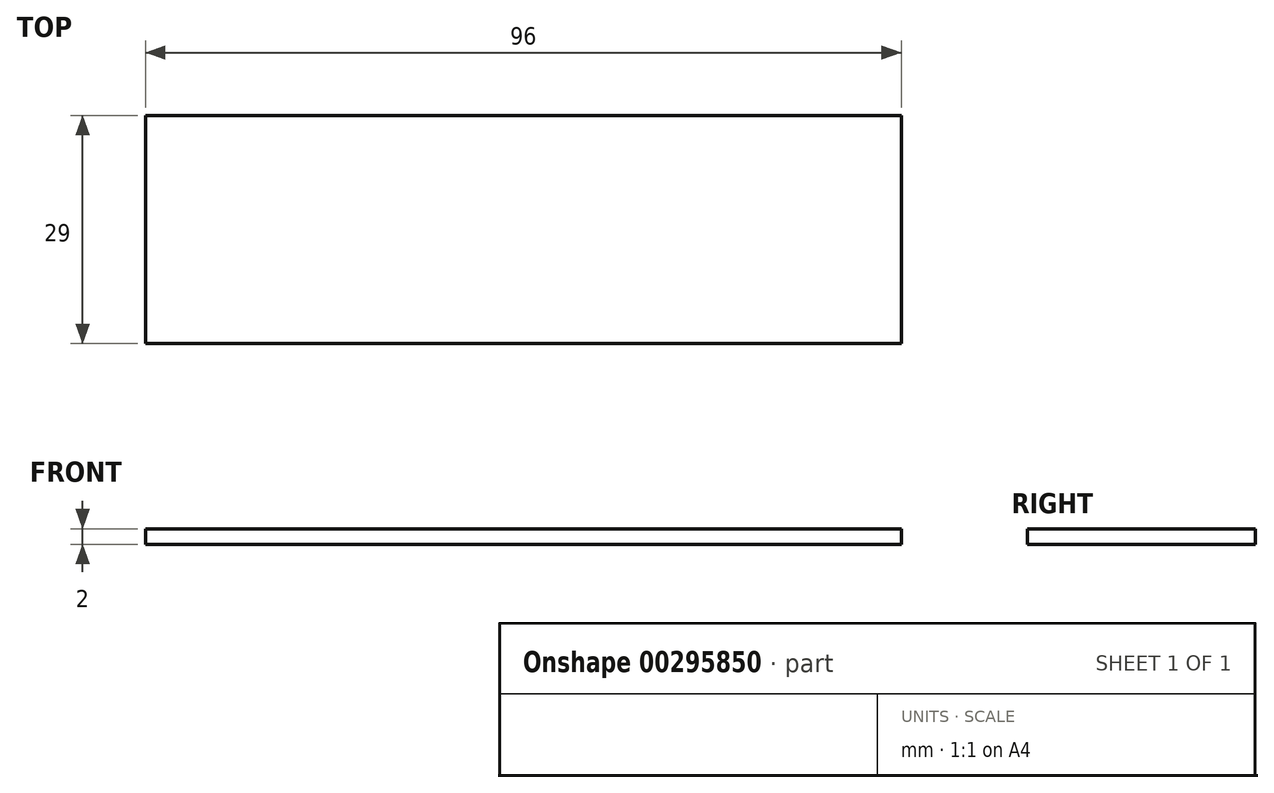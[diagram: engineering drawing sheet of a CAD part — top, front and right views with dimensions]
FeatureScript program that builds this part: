
annotation { "Feature Type Name" : "Feature", "Feature Type Description" : "" }
export const myFeature = defineFeature(function(context is Context, id is Id, definition is map)
    precondition{}
    {
        {
            var Q0;
            Q0=qCreatedBy(makeId("Top.planeOp"),FACE);
            var sketch = newSketch(context, id + "F0", { "sketchPlane" : qUnion([Q0])});
            skLineSegment(sketch, "E0.bottom", {"start": v(-48, 14.5) * mm, "end": v(48, 14.5) * mm});
            skLineSegment(sketch, "E0.top", {"start": v(-48, -14.5) * mm, "end": v(48, -14.5) * mm});
            skLineSegment(sketch, "E0.left", {"start": v(-48, 14.5) * mm, "end": v(-48, -14.5) * mm});
            skLineSegment(sketch, "E0.right", {"start": v(48, 14.5) * mm, "end": v(48, -14.5) * mm});
            skPoint(sketch, "E0.middle", {"position": v(0, 0) * mm});
            skSolve(sketch);
        }
        {
            var Q0;
            Q0 = qSketchRegion(id + "F0", true);
            extrude(context, id + "F1", {"entities" : qUnion([Q0]), "depth" : 2 * mm, "offsetDistance" : 25 * mm});
        }
    });
